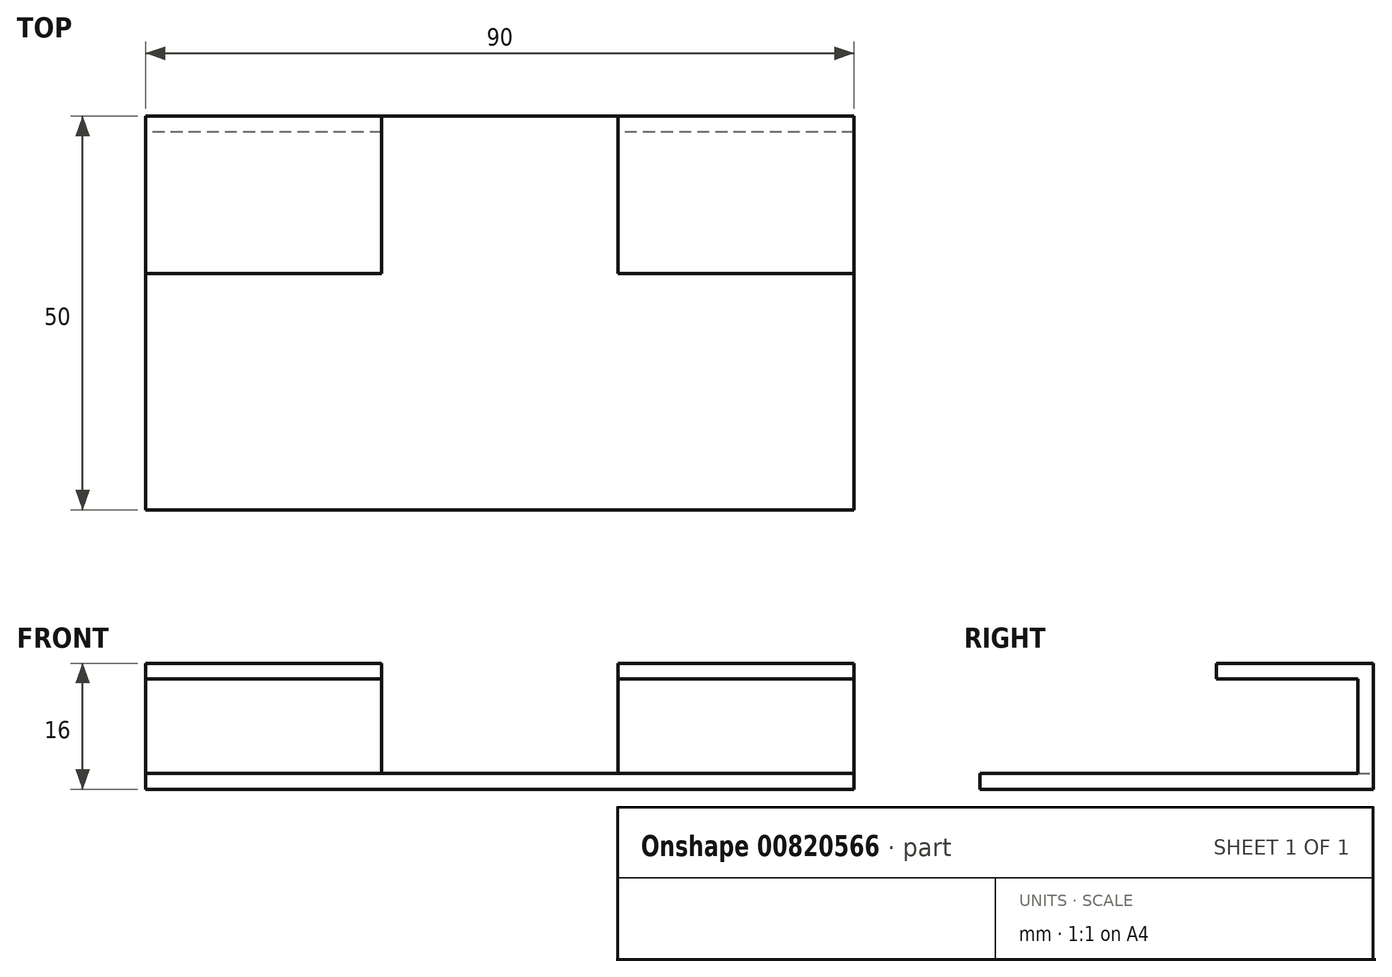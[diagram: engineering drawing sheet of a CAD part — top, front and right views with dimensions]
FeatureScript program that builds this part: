
annotation { "Feature Type Name" : "Feature", "Feature Type Description" : "" }
export const myFeature = defineFeature(function(context is Context, id is Id, definition is map)
    precondition{}
    {
        {
            var Q0;
            Q0=qCreatedBy(makeId("Right.planeOp"),FACE);
            var sketch = newSketch(context, id + "F0", { "sketchPlane" : qUnion([Q0])});
            skLineSegment(sketch, "E0.bottom", {"start": v(0, 0) * mm, "end": v(50, 0) * mm});
            skLineSegment(sketch, "E0.top", {"start": v(0, -2) * mm, "end": v(50, -2) * mm});
            skLineSegment(sketch, "E0.left", {"start": v(0, 0) * mm, "end": v(0, -2) * mm});
            skLineSegment(sketch, "E0.right", {"start": v(50, 0) * mm, "end": v(50, -2) * mm});
            skLineSegment(sketch, "E1.bottom", {"start": v(50, 0) * mm, "end": v(48, 0) * mm});
            skLineSegment(sketch, "E1.top", {"start": v(50, 12) * mm, "end": v(48, 12) * mm});
            skLineSegment(sketch, "E1.left", {"start": v(50, 0) * mm, "end": v(50, 12) * mm});
            skLineSegment(sketch, "E1.right", {"start": v(48, 0) * mm, "end": v(48, 12) * mm});
            skLineSegment(sketch, "E2.bottom", {"start": v(50, 12) * mm, "end": v(30, 12) * mm});
            skLineSegment(sketch, "E2.top", {"start": v(50, 14) * mm, "end": v(30, 14) * mm});
            skLineSegment(sketch, "E2.left", {"start": v(50, 12) * mm, "end": v(50, 14) * mm});
            skLineSegment(sketch, "E2.right", {"start": v(30, 12) * mm, "end": v(30, 14) * mm});
            skSolve(sketch);
        }
        {
            var Q0;
            Q0 = qSketchRegion(id + "F0", true);
            extrude(context, id + "F1", {"entities" : qUnion([Q0]), "endBound" : BoundingType.SYMMETRIC, "depth" : 90 * mm, "offsetDistance" : 25 * mm});
        }
        {
            var Q0;
            Q0=makeQuery(id+"F1.opExtrude","SWEPT_FACE",FACE,{"disambiguationData":[OSD([sQuery(id+"F0.wireOp",EDGE,"E2.top")])]});
            var sketch = newSketch(context, id + "F2", { "sketchPlane" : qUnion([Q0])});
            skLineSegment(sketch, "E3.bottom", {"start": v(-15, 30) * mm, "end": v(15, 30) * mm});
            skLineSegment(sketch, "E3.top", {"start": v(-15, 50) * mm, "end": v(15, 50) * mm});
            skLineSegment(sketch, "E3.left", {"start": v(-15, 30) * mm, "end": v(-15, 50) * mm});
            skLineSegment(sketch, "E3.right", {"start": v(15, 30) * mm, "end": v(15, 50) * mm});
            skSolve(sketch);
        }
        {
            var Q0;
            Q0=makeQuery(id+"F2.imprint","IMPRINT",FACE,{"disambiguationData":[TD([[makeQuery(id+"F2.imprint","IMPRINT",EDGE,{"derivedFrom":sQuery(id+"F2.wireOp",EDGE,"E3.bottom")}),-1.0]])]});
            extrude(context, id + "F3", {"entities" : qUnion([Q0]), "operationType" : NewBodyOperationType.REMOVE, "oppositeDirection" : true, "depth" : 14 * mm, "offsetDistance" : 25 * mm});
        }
    });
